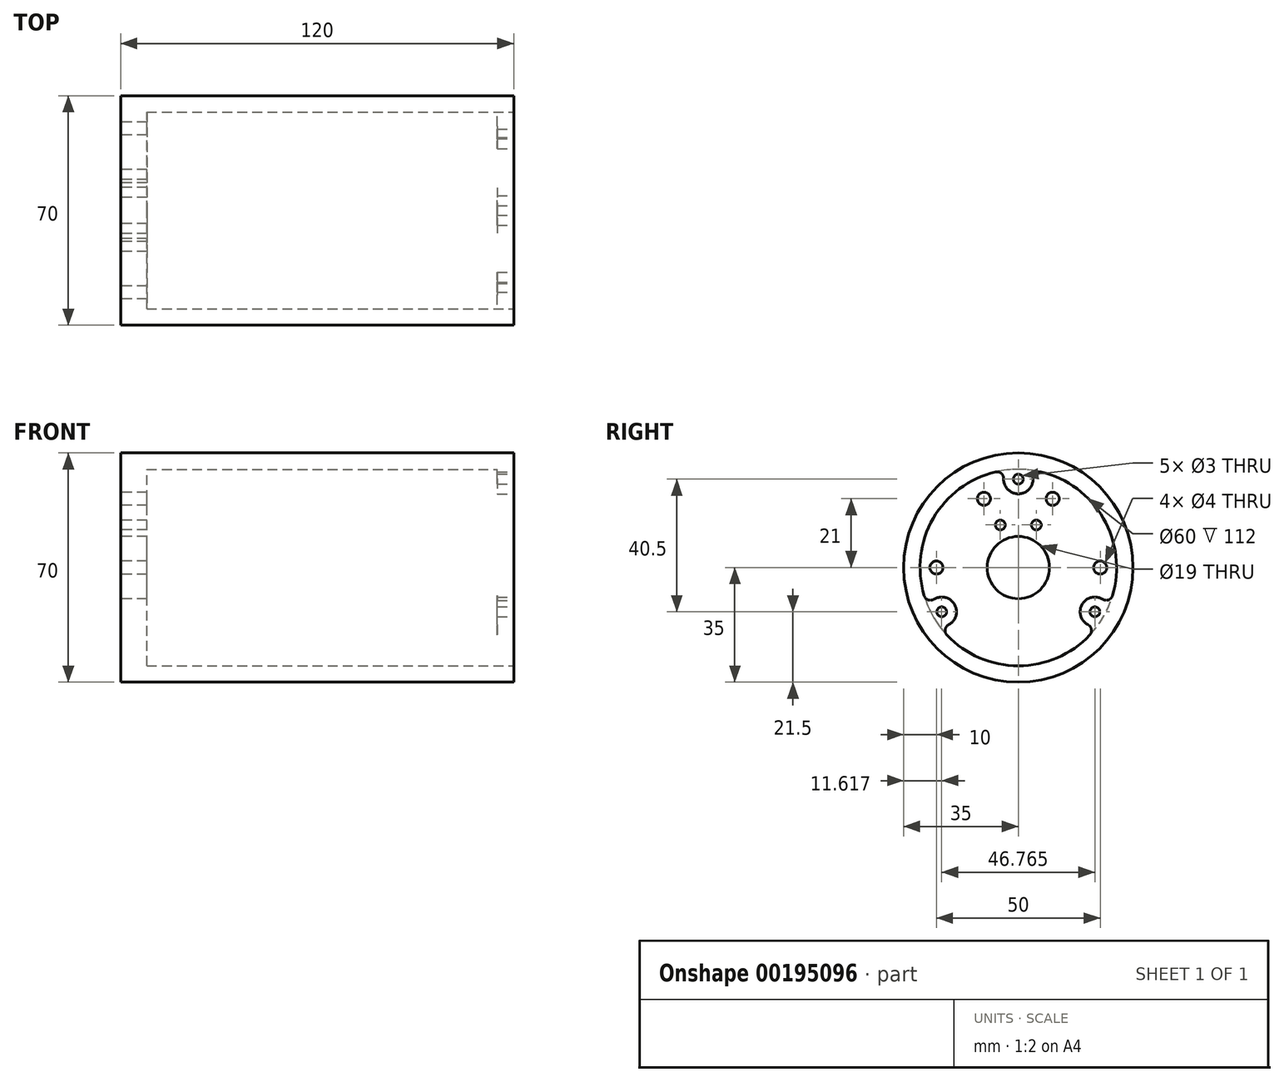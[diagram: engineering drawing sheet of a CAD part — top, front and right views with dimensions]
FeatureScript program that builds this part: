
annotation { "Feature Type Name" : "Feature", "Feature Type Description" : "" }
export const myFeature = defineFeature(function(context is Context, id is Id, definition is map)
    precondition{}
    {
        {
            var Q0;
            Q0=qCreatedBy(makeId("Right.planeOp"),FACE);
            var sketch = newSketch(context, id + "F0", { "sketchPlane" : qUnion([Q0])});
            skCircle(sketch, "E0", {"center": v(0, 0) * mm, "radius": 35 * mm});
            skSolve(sketch);
        }
        {
            var Q0;
            Q0 = qSketchRegion(id + "F0", true);
            extrude(context, id + "F1", {"entities" : qUnion([Q0]), "depth" : 120 * mm});
        }
        {
            var Q0;
            Q0=makeQuery(id+"F1.opExtrude","CAP_FACE",FACE,{"disambiguationData":[OSD([sQuery(id+"F0.wireOp",EDGE,"E0")])],"isStart":false});
            var sketch = newSketch(context, id + "F2", { "sketchPlane" : qUnion([Q0])});
            skArc(sketch, "E1.0", {"start": v(-21.8, -20.62) * mm, "mid": v(0, -30) * mm, "end": v(21.8, -20.62) * mm});
            skLineSegment(sketch, "E2", {"start": v(0, 0) * mm, "end": v(0, 55.34) * mm, "construction": true});
            skLineSegment(sketch, "E3", {"start": v(0, 0) * mm, "end": v(45.7, -26.39) * mm, "construction": true});
            skLineSegment(sketch, "E4", {"start": v(0, 0) * mm, "end": v(-42.11, -24.31) * mm, "construction": true});
            skCircle(sketch, "E5", {"center": v(0, 0) * mm, "radius": 27 * mm, "construction": true});
            skArc(sketch, "E6", {"start": v(-4.5, 27.16) * mm, "mid": v(0, 22.5) * mm, "end": v(4.5, 27.16) * mm});
            skArc(sketch, "E7", {"start": v(25.77, -9.69) * mm, "mid": v(19.49, -11.25) * mm, "end": v(21.28, -17.48) * mm});
            skArc(sketch, "E8", {"start": v(-21.28, -17.48) * mm, "mid": v(-19.49, -11.25) * mm, "end": v(-25.77, -9.69) * mm});
            skArc(sketch, "E9", {"start": v(-4.6, 26.6) * mm, "mid": v(-5.02, 28.59) * mm, "end": v(-6.96, 29.18) * mm});
            skArc(sketch, "E10", {"start": v(6.96, 29.18) * mm, "mid": v(5.02, 28.59) * mm, "end": v(4.6, 26.6) * mm});
            skArc(sketch, "E11.1.0", {"start": v(-28.75, -8.56) * mm, "mid": v(-27.27, -9.95) * mm, "end": v(-25.34, -9.32) * mm});
            skArc(sketch, "E11.1.1", {"start": v(-20.74, -17.28) * mm, "mid": v(-22.25, -18.64) * mm, "end": v(-21.8, -20.62) * mm});
            skArc(sketch, "E11.2.0", {"start": v(21.8, -20.62) * mm, "mid": v(22.25, -18.64) * mm, "end": v(20.74, -17.28) * mm});
            skArc(sketch, "E11.2.1", {"start": v(25.34, -9.32) * mm, "mid": v(27.27, -9.95) * mm, "end": v(28.75, -8.56) * mm});
            skArc(sketch, "E12.trimOffspring", {"start": v(28.75, -8.56) * mm, "mid": v(25.98, 15) * mm, "end": v(6.96, 29.18) * mm});
            skArc(sketch, "E13.trimOffspring", {"start": v(-6.96, 29.18) * mm, "mid": v(-25.98, 15) * mm, "end": v(-28.75, -8.56) * mm});
            skSolve(sketch);
        }
        {
            var Q0;
            {var subQ1=sQuery(id+"F2.wireOp",EDGE,"E1.0");Q0=makeQuery(id+"F2.imprint","IMPRINT",FACE,{"disambiguationData":[TD([[makeQuery(id+"F2.imprint","IMPRINT",EDGE,{"derivedFrom":subQ1}),1.0]])]});}
            extrude(context, id + "F3", {"entities" : qUnion([Q0]), "operationType" : NewBodyOperationType.REMOVE, "oppositeDirection" : true, "depth" : 5 * mm});
        }
        {
            var Q0;
            Q0=makeQuery(id+"F3.boolean.opBoolean","COPY",FACE,{"derivedFrom":makeQuery(id+"F3.opExtrude","CAP_FACE",FACE,{"disambiguationData":[OSD([sQuery(id+"F2.wireOp",EDGE,"E1.0"),sQuery(id+"F2.wireOp",EDGE,"E6"),sQuery(id+"F2.wireOp",EDGE,"E7"),sQuery(id+"F2.wireOp",EDGE,"E8"),sQuery(id+"F2.wireOp",EDGE,"E9"),sQuery(id+"F2.wireOp",EDGE,"E10"),sQuery(id+"F2.wireOp",EDGE,"E11.1.0"),sQuery(id+"F2.wireOp",EDGE,"E11.1.1"),sQuery(id+"F2.wireOp",EDGE,"E11.2.0"),sQuery(id+"F2.wireOp",EDGE,"E11.2.1"),sQuery(id+"F2.wireOp",EDGE,"E12.trimOffspring"),sQuery(id+"F2.wireOp",EDGE,"E13.trimOffspring")])],"isStart":false})});
            var sketch = newSketch(context, id + "F4", { "sketchPlane" : qUnion([Q0])});
            skCircle(sketch, "E14", {"center": v(0, 0) * mm, "radius": 30 * mm});
            skSolve(sketch);
        }
        {
            var Q0;
            Q0 = qSketchRegion(id + "F4", true);
            extrude(context, id + "F5", {"entities" : qUnion([Q0]), "operationType" : NewBodyOperationType.REMOVE, "oppositeDirection" : true, "depth" : 107 * mm});
        }
        {
            var Q0;
            Q0=makeQuery(id+"F1.opExtrude","CAP_FACE",FACE,{"disambiguationData":[OSD([sQuery(id+"F0.wireOp",EDGE,"E0")])],"isStart":false});
            var sketch = newSketch(context, id + "F6", { "sketchPlane" : qUnion([Q0])});
            skPoint(sketch, "E15", {"position": v(-23.38, -13.5) * mm});
            skPoint(sketch, "E16", {"position": v(0, 27) * mm});
            skPoint(sketch, "E17", {"position": v(23.38, -13.5) * mm});
            skSolve(sketch);
        }
        {
            var Q0;
            Q0=sQuery(id+"F6.wireOp",VERTEX,"E15");
            var Q1;
            Q1=sQuery(id+"F6.wireOp",VERTEX,"E16");
            var Q2;
            Q2=sQuery(id+"F6.wireOp",VERTEX,"E17");
            var Q3;
            Q3=makeQuery(id+"F1.opExtrude","SWEPT_BODY",BODY,{"disambiguationData":[OSD([sQuery(id+"F0.wireOp",EDGE,"E0")])]});
            hole(context, id + "F7", {"style" : HoleStyle.SIMPLE, "endStyle" : HoleEndStyle.BLIND, "standardTappedOrClearance" : lookupTablePath({ "standard" : "ISO", "size" : "3", "type" : "Drilled" }), "standardBlindInLast" : lookupTablePath({ "standard" : "ISO", "size" : "3", "type" : "Drilled" }), "holeDiameter" : 3 * mm, "holeDepth" : 6 * mm, "locations" : qUnion([Q0, Q1, Q2]), "scope" : qUnion([Q3])});
        }
        {
            var Q0;
            Q0=makeQuery(id+"F1.opExtrude","CAP_FACE",FACE,{"disambiguationData":[OSD([sQuery(id+"F0.wireOp",EDGE,"E0")])],"isStart":true});
            var sketch = newSketch(context, id + "F8", { "sketchPlane" : qUnion([Q0])});
            skLineSegment(sketch, "E18", {"start": v(0, 0) * mm, "end": v(125.9, 0) * mm, "construction": true});
            skLineSegment(sketch, "E19", {"start": v(0, 0) * mm, "end": v(-125.96, 0) * mm, "construction": true});
            skPoint(sketch, "E20", {"position": v(-25, 0) * mm});
            skPoint(sketch, "E21", {"position": v(25, 0) * mm});
            skPoint(sketch, "E22", {"position": v(0, 0) * mm});
            skSolve(sketch);
        }
        {
            var Q0;
            Q0=sQuery(id+"F8.wireOp",VERTEX,"E20");
            var Q1;
            Q1=sQuery(id+"F8.wireOp",VERTEX,"E21");
            var Q2;
            Q2=makeQuery(id+"F1.opExtrude","SWEPT_BODY",BODY,{"disambiguationData":[OSD([sQuery(id+"F0.wireOp",EDGE,"E0")])]});
            hole(context, id + "F9", {"style" : HoleStyle.SIMPLE, "endStyle" : HoleEndStyle.BLIND, "standardTappedOrClearance" : lookupTablePath({ "standard" : "ISO", "size" : "4", "type" : "Drilled" }), "standardBlindInLast" : lookupTablePath({ "standard" : "ISO", "size" : "4", "type" : "Drilled" }), "holeDiameter" : 4 * mm, "holeDepth" : 10 * mm, "locations" : qUnion([Q0, Q1]), "scope" : qUnion([Q2])});
        }
        {
            var Q0;
            Q0=makeQuery(id+"F1.opExtrude","CAP_FACE",FACE,{"disambiguationData":[OSD([sQuery(id+"F0.wireOp",EDGE,"E0")])],"isStart":true});
            var sketch = newSketch(context, id + "F10", { "sketchPlane" : qUnion([Q0])});
            skCircle(sketch, "E23", {"center": v(0, 0) * mm, "radius": 9.5 * mm});
            skSolve(sketch);
        }
        {
            var Q0;
            Q0=makeQuery(id+"F10.imprint","IMPRINT",FACE,{"disambiguationData":[TD([[makeQuery(id+"F10.imprint","IMPRINT",EDGE,{"derivedFrom":sQuery(id+"F10.wireOp",EDGE,"E23")}),1.0]])]});
            extrude(context, id + "F11", {"entities" : qUnion([Q0]), "operationType" : NewBodyOperationType.REMOVE, "oppositeDirection" : true, "depth" : 25 * mm});
        }
        {
            var Q0;
            Q0=makeQuery(id+"F1.opExtrude","CAP_FACE",FACE,{"disambiguationData":[OSD([sQuery(id+"F0.wireOp",EDGE,"E0")])],"isStart":true});
            var sketch = newSketch(context, id + "F12", { "sketchPlane" : qUnion([Q0])});
            skLineSegment(sketch, "E24", {"start": v(0, 0) * mm, "end": v(0, 31.76) * mm, "construction": true});
            skLineSegment(sketch, "E25", {"start": v(0, 0) * mm, "end": v(40.02, 0) * mm, "construction": true});
            skPoint(sketch, "E26", {"position": v(10.5, 21) * mm});
            skPoint(sketch, "E27", {"position": v(-10.5, 21) * mm});
            skSolve(sketch);
        }
        {
            var Q0;
            Q0=sQuery(id+"F12.wireOp",VERTEX,"E27");
            var Q1;
            Q1=sQuery(id+"F12.wireOp",VERTEX,"E26");
            var Q2;
            Q2=makeQuery(id+"F1.opExtrude","SWEPT_BODY",BODY,{"disambiguationData":[OSD([sQuery(id+"F0.wireOp",EDGE,"E0")])]});
            hole(context, id + "F13", {"style" : HoleStyle.SIMPLE, "endStyle" : HoleEndStyle.BLIND, "standardTappedOrClearance" : lookupTablePath({ "standard" : "ISO", "size" : "4", "type" : "Drilled" }), "standardBlindInLast" : lookupTablePath({ "standard" : "ISO", "size" : "4", "type" : "Drilled" }), "holeDiameter" : 4 * mm, "holeDepth" : 10 * mm, "locations" : qUnion([Q0, Q1]), "scope" : qUnion([Q2])});
        }
        {
            var Q0;
            Q0=makeQuery(id+"F1.opExtrude","CAP_FACE",FACE,{"disambiguationData":[OSD([sQuery(id+"F0.wireOp",EDGE,"E0")])],"isStart":true});
            var sketch = newSketch(context, id + "F14", { "sketchPlane" : qUnion([Q0])});
            skPoint(sketch, "E28", {"position": v(5.5, 13) * mm});
            skPoint(sketch, "E29", {"position": v(-5.5, 13) * mm});
            skLineSegment(sketch, "E30", {"start": v(0, 0) * mm, "end": v(0, 33.73) * mm, "construction": true});
            skLineSegment(sketch, "E31", {"start": v(0, 0) * mm, "end": v(59.72, 0) * mm, "construction": true});
            skSolve(sketch);
        }
        {
            var Q0;
            Q0=sQuery(id+"F14.wireOp",VERTEX,"E29");
            var Q1;
            Q1=sQuery(id+"F14.wireOp",VERTEX,"E28");
            var Q2;
            Q2=makeQuery(id+"F1.opExtrude","SWEPT_BODY",BODY,{"disambiguationData":[OSD([sQuery(id+"F0.wireOp",EDGE,"E0")])]});
            hole(context, id + "F15", {"style" : HoleStyle.SIMPLE, "endStyle" : HoleEndStyle.THROUGH, "holeDiameter" : 3 * mm, "locations" : qUnion([Q0, Q1]), "scope" : qUnion([Q2]), "isTappedThrough" : true});
        }
    });
